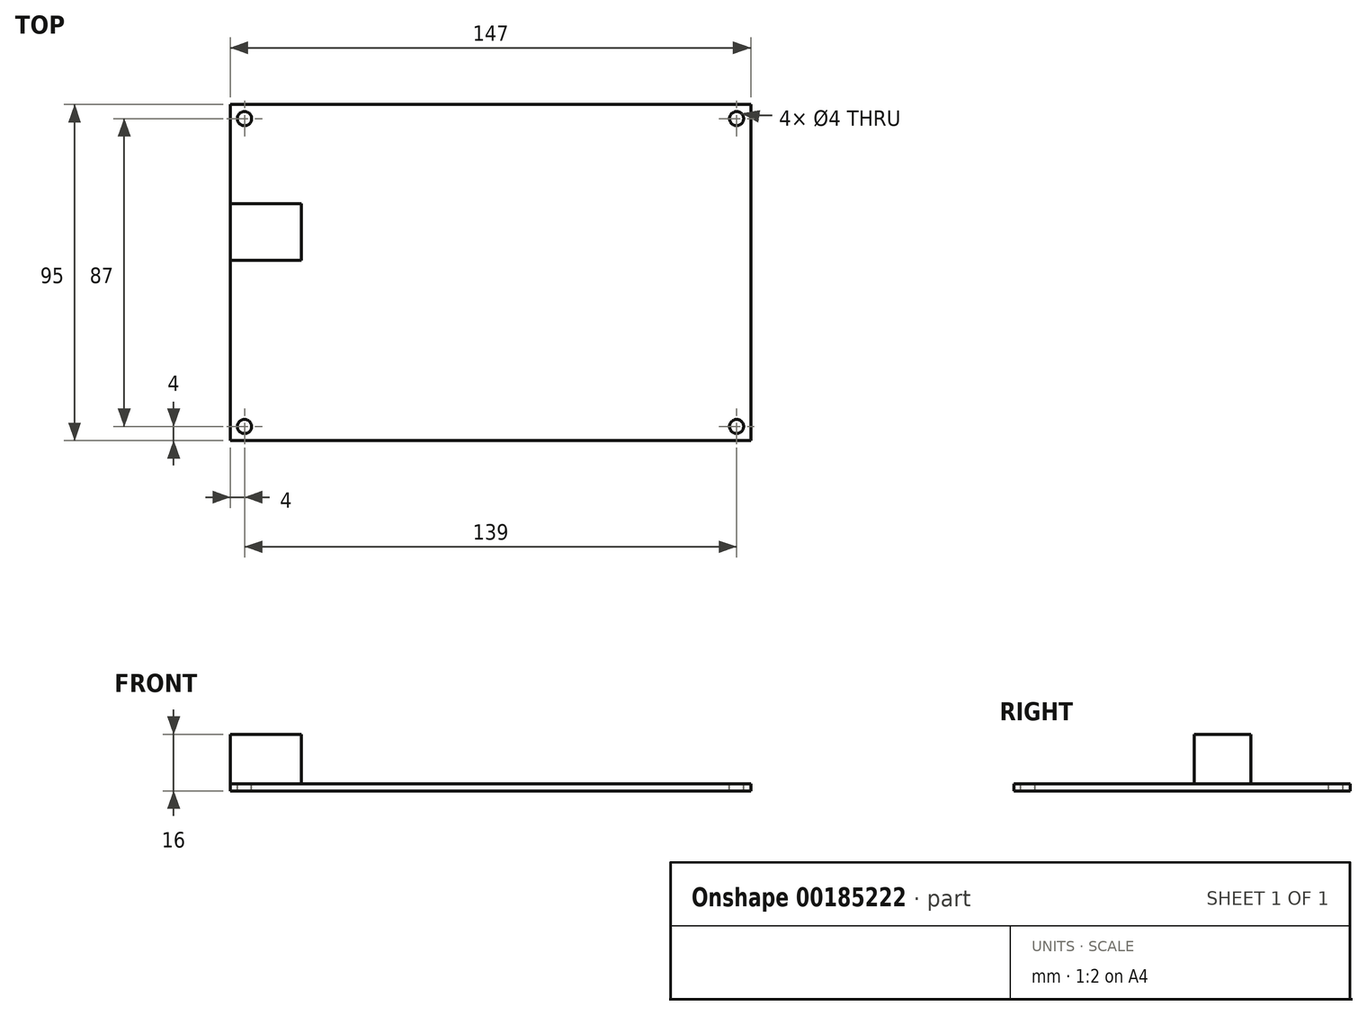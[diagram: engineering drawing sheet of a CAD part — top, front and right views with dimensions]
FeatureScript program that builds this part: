
annotation { "Feature Type Name" : "Feature", "Feature Type Description" : "" }
export const myFeature = defineFeature(function(context is Context, id is Id, definition is map)
    precondition{}
    {
        {
            var Q0;
            Q0=qCreatedBy(makeId("Top.planeOp"),FACE);
            var sketch = newSketch(context, id + "F0", { "sketchPlane" : qUnion([Q0])});
            skLineSegment(sketch, "E0.bottom", {"start": v(73.5, -47.5) * mm, "end": v(-73.5, -47.5) * mm});
            skLineSegment(sketch, "E0.top", {"start": v(73.5, 47.5) * mm, "end": v(-73.5, 47.5) * mm});
            skLineSegment(sketch, "E0.left", {"start": v(73.5, -47.5) * mm, "end": v(73.5, 47.5) * mm});
            skLineSegment(sketch, "E0.right", {"start": v(-73.5, -47.5) * mm, "end": v(-73.5, 47.5) * mm});
            skPoint(sketch, "E0.middle", {"position": v(0, 0) * mm});
            skCircle(sketch, "E1", {"center": v(-69.5, 43.5) * mm, "radius": 2 * mm});
            skCircle(sketch, "E2.MirrorC", {"center": v(69.5, 43.5) * mm, "radius": 2 * mm});
            skCircle(sketch, "E3.MirrorC", {"center": v(69.5, -43.5) * mm, "radius": 2 * mm});
            skCircle(sketch, "E4.MirrorC", {"center": v(-69.5, -43.5) * mm, "radius": 2 * mm});
            skLineSegment(sketch, "E5.bottom", {"start": v(-73.5, 19.5) * mm, "end": v(-53.5, 19.5) * mm});
            skLineSegment(sketch, "E5.top", {"start": v(-73.5, 3.5) * mm, "end": v(-53.5, 3.5) * mm});
            skLineSegment(sketch, "E5.left", {"start": v(-73.5, 19.5) * mm, "end": v(-73.5, 3.5) * mm});
            skLineSegment(sketch, "E5.right", {"start": v(-53.5, 19.5) * mm, "end": v(-53.5, 3.5) * mm});
            skPoint(sketch, "E5.middle", {"position": v(-63.5, 11.5) * mm});
            skSolve(sketch);
        }
        {
            var Q0;
            {var subQ4=sQuery(id+"F0.wireOp",EDGE,"E0.bottom");Q0=makeQuery(id+"F0.imprint","IMPRINT",FACE,{"disambiguationData":[TD([[makeQuery(id+"F0.imprint","IMPRINT",EDGE,{"derivedFrom":subQ4}),-1.0]])]});}
            var Q1;
            Q1=makeQuery(id+"F0.imprint","IMPRINT",FACE,{"disambiguationData":[TD([[makeQuery(id+"F0.imprint","IMPRINT",EDGE,{"derivedFrom":sQuery(id+"F0.wireOp",EDGE,"E5.bottom")}),-1.0]])]});
            extrude(context, id + "F1", {"entities" : qUnion([Q0, Q1]), "oppositeDirection" : true, "depth" : 2 * mm, "offsetDistance" : 25 * mm});
        }
        {
            var Q0;
            Q0=makeQuery(id+"F0.imprint","IMPRINT",FACE,{"disambiguationData":[TD([[makeQuery(id+"F0.imprint","IMPRINT",EDGE,{"derivedFrom":sQuery(id+"F0.wireOp",EDGE,"E5.bottom")}),-1.0]])]});
            extrude(context, id + "F2", {"entities" : qUnion([Q0]), "operationType" : NewBodyOperationType.ADD, "depth" : 14 * mm, "offsetDistance" : 25 * mm});
        }
    });
